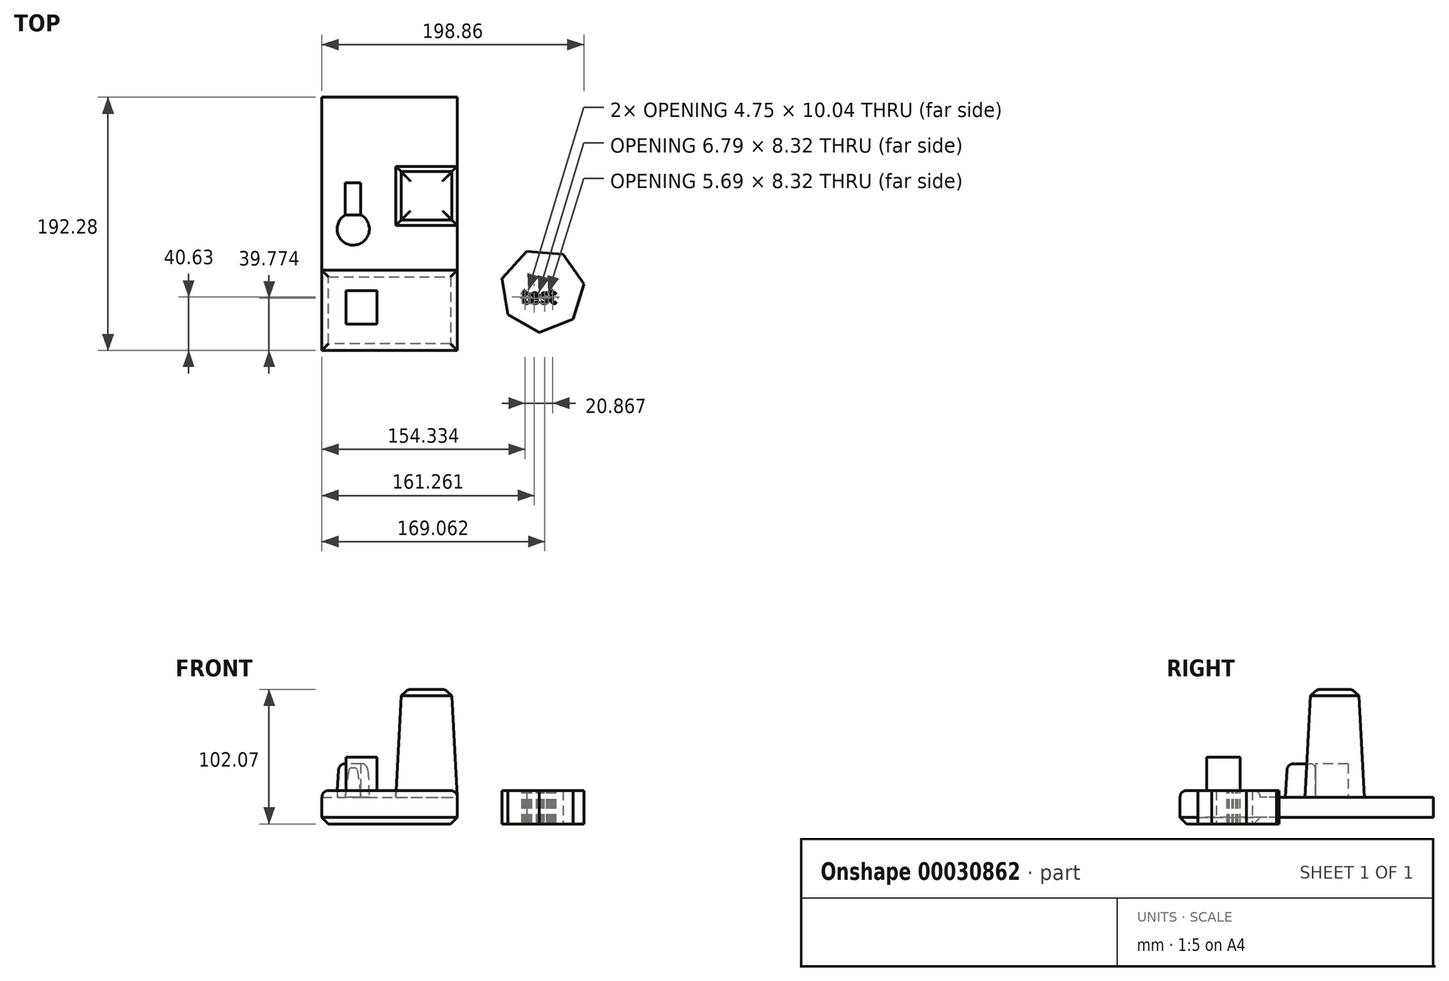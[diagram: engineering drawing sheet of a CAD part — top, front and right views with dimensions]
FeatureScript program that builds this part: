
annotation { "Feature Type Name" : "Feature", "Feature Type Description" : "" }
export const myFeature = defineFeature(function(context is Context, id is Id, definition is map)
    precondition{}
    {
        {
            var Q0;
            Q0=qCreatedBy(makeId("Top.planeOp"),FACE);
            var sketch = newSketch(context, id + "F0", { "sketchPlane" : qUnion([Q0])});
            skLineSegment(sketch, "E0.bottom", {"start": v(-102.72, 60.89) * mm, "end": v(0, 60.89) * mm});
            skLineSegment(sketch, "E0.top", {"start": v(-102.72, 0) * mm, "end": v(0, 0) * mm});
            skLineSegment(sketch, "E0.left", {"start": v(-102.72, 60.89) * mm, "end": v(-102.72, 0) * mm});
            skLineSegment(sketch, "E0.right", {"start": v(0, 60.89) * mm, "end": v(0, 0) * mm});
            skSolve(sketch);
        }
        {
            var Q0;
            Q0 = qSketchRegion(id + "F0", true);
            extrude(context, id + "F1", {"entities" : qUnion([Q0]), "depth" : 25.4 * mm});
        }
        {
            var Q0;
            Q0=makeQuery(id+"F1.opExtrude","CAP_EDGE",EDGE,{"disambiguationData":[OSD([sQuery(id+"F0.wireOp",EDGE,"E0.top")])],"isStart":false});
            var Q1;
            Q1=makeQuery(id+"F1.opExtrude","CAP_EDGE",EDGE,{"disambiguationData":[OSD([sQuery(id+"F0.wireOp",EDGE,"E0.left")])],"isStart":false});
            var Q2;
            Q2=makeQuery(id+"F1.opExtrude","CAP_EDGE",EDGE,{"disambiguationData":[OSD([sQuery(id+"F0.wireOp",EDGE,"E0.bottom")])],"isStart":false});
            var Q3;
            Q3=makeQuery(id+"F1.opExtrude","CAP_EDGE",EDGE,{"disambiguationData":[OSD([sQuery(id+"F0.wireOp",EDGE,"E0.right")])],"isStart":false});
            fillet(context, id + "F2", {"entities" : qUnion([Q0, Q1, Q2, Q3]), "radius" : 5.08 * mm, "tangentPropagation" : true, "allowEdgeOverflow" : false});
        }
        {
            var Q0;
            Q0=makeQuery(id+"F1.opExtrude","CAP_EDGE",EDGE,{"disambiguationData":[OSD([sQuery(id+"F0.wireOp",EDGE,"E0.top")])],"isStart":true});
            var Q1;
            Q1=makeQuery(id+"F1.opExtrude","CAP_FACE",FACE,{"disambiguationData":[OSD([sQuery(id+"F0.wireOp",EDGE,"E0.bottom"),sQuery(id+"F0.wireOp",EDGE,"E0.top"),sQuery(id+"F0.wireOp",EDGE,"E0.left"),sQuery(id+"F0.wireOp",EDGE,"E0.right")])],"isStart":true});
            chamfer(context, id + "F3", {"entities" : qUnion([Q0, Q1]), "width" : 5.08 * mm, "tangentPropagation" : true});
        }
        {
            var Q0;
            Q0=makeQuery(id+"F1.opExtrude","SWEPT_FACE",FACE,{"disambiguationData":[OSD([sQuery(id+"F0.wireOp",EDGE,"E0.bottom")])]});
            extrude(context, id + "F4", {"entities" : qUnion([Q0]), "operationType" : NewBodyOperationType.ADD, "depth" : 131.4 * mm});
        }
        {
            var Q0;
            {var subQ0=sQuery(id+"F0.wireOp",EDGE,"E0.bottom");Q0=makeQuery(id+"F4.opExtrude","SWEPT_FACE",FACE,{"disambiguationData":[OSD([subQ0]),TDD([makeQuery(id+"F2.opFillet","BLEND_EDGE",EDGE,{"blendedFrom":[makeQuery(id+"F1.opExtrude","CAP_EDGE",EDGE,{"disambiguationData":[OSD([subQ0])],"isStart":false}),makeQuery(id+"F1.opExtrude","SWEPT_FACE",FACE,{"disambiguationData":[OSD([subQ0])]})],"blendedInto":[makeQuery(id+"F1.opExtrude","SWEPT_FACE",FACE,{"disambiguationData":[OSD([subQ0])]})]})])]});}
            var sketch = newSketch(context, id + "F5", { "sketchPlane" : qUnion([Q0])});
            skLineSegment(sketch, "E1.bottom", {"start": v(-46.64, 139.86) * mm, "end": v(0, 139.86) * mm});
            skLineSegment(sketch, "E1.top", {"start": v(-46.64, 94.95) * mm, "end": v(0, 94.95) * mm});
            skLineSegment(sketch, "E1.left", {"start": v(0, 139.86) * mm, "end": v(0, 94.95) * mm});
            skLineSegment(sketch, "E1.right", {"start": v(-46.64, 139.86) * mm, "end": v(-46.64, 94.95) * mm});
            skSolve(sketch);
        }
        {
            var Q0;
            Q0 = qSketchRegion(id + "F5", true);
            extrude(context, id + "F6", {"entities" : qUnion([Q0]), "operationType" : NewBodyOperationType.ADD, "depth" : 81.75 * mm, "hasDraft" : true, "draftAngle" : 3 * degree, "draftPullDirection" : true});
        }
        {
            var Q0;
            Q0=makeQuery(id+"F6.opExtrude","CAP_EDGE",EDGE,{"disambiguationData":[OSD([sQuery(id+"F5.wireOp",EDGE,"E1.left")])],"isStart":false});
            var Q1;
            Q1=makeQuery(id+"F6.opExtrude","CAP_EDGE",EDGE,{"disambiguationData":[OSD([sQuery(id+"F5.wireOp",EDGE,"E1.top")])],"isStart":false});
            var Q2;
            Q2=makeQuery(id+"F6.opExtrude","CAP_EDGE",EDGE,{"disambiguationData":[OSD([sQuery(id+"F5.wireOp",EDGE,"E1.right")])],"isStart":false});
            var Q3;
            Q3=makeQuery(id+"F6.opExtrude","CAP_EDGE",EDGE,{"disambiguationData":[OSD([sQuery(id+"F5.wireOp",EDGE,"E1.bottom")])],"isStart":false});
            chamfer(context, id + "F7", {"entities" : qUnion([Q0, Q1, Q2, Q3]), "width" : 5.08 * mm, "tangentPropagation" : true});
        }
        {
            var Q0;
            {var subQ0=sQuery(id+"F5.wireOp",EDGE,"E1.top");Q0=makeQuery(id+"F7.opChamfer","BLEND_EDGE",EDGE,{"blendedFrom":[makeQuery(id+"F6.opExtrude","CAP_EDGE",EDGE,{"disambiguationData":[OSD([subQ0])],"isStart":false}),makeQuery(id+"F6.opExtrude","CAP_FACE",FACE,{"disambiguationData":[OSD([sQuery(id+"F5.wireOp",EDGE,"E1.bottom"),subQ0,sQuery(id+"F5.wireOp",EDGE,"E1.left"),sQuery(id+"F5.wireOp",EDGE,"E1.right")])],"isStart":false})],"blendedInto":[makeQuery(id+"F6.opExtrude","CAP_FACE",FACE,{"disambiguationData":[OSD([sQuery(id+"F5.wireOp",EDGE,"E1.bottom"),subQ0,sQuery(id+"F5.wireOp",EDGE,"E1.left"),sQuery(id+"F5.wireOp",EDGE,"E1.right")])],"isStart":false})]});}
            var Q1;
            {var subQ0=sQuery(id+"F5.wireOp",EDGE,"E1.left");Q1=makeQuery(id+"F7.opChamfer","BLEND_EDGE",EDGE,{"blendedFrom":[makeQuery(id+"F6.opExtrude","CAP_EDGE",EDGE,{"disambiguationData":[OSD([subQ0])],"isStart":false}),makeQuery(id+"F6.opExtrude","CAP_FACE",FACE,{"disambiguationData":[OSD([sQuery(id+"F5.wireOp",EDGE,"E1.bottom"),sQuery(id+"F5.wireOp",EDGE,"E1.top"),subQ0,sQuery(id+"F5.wireOp",EDGE,"E1.right")])],"isStart":false})],"blendedInto":[makeQuery(id+"F6.opExtrude","CAP_FACE",FACE,{"disambiguationData":[OSD([sQuery(id+"F5.wireOp",EDGE,"E1.bottom"),sQuery(id+"F5.wireOp",EDGE,"E1.top"),subQ0,sQuery(id+"F5.wireOp",EDGE,"E1.right")])],"isStart":false})]});}
            var Q2;
            {var subQ0=sQuery(id+"F5.wireOp",EDGE,"E1.bottom");Q2=makeQuery(id+"F7.opChamfer","BLEND_EDGE",EDGE,{"blendedFrom":[makeQuery(id+"F6.opExtrude","CAP_EDGE",EDGE,{"disambiguationData":[OSD([subQ0])],"isStart":false}),makeQuery(id+"F6.opExtrude","CAP_FACE",FACE,{"disambiguationData":[OSD([subQ0,sQuery(id+"F5.wireOp",EDGE,"E1.top"),sQuery(id+"F5.wireOp",EDGE,"E1.left"),sQuery(id+"F5.wireOp",EDGE,"E1.right")])],"isStart":false})],"blendedInto":[makeQuery(id+"F6.opExtrude","CAP_FACE",FACE,{"disambiguationData":[OSD([subQ0,sQuery(id+"F5.wireOp",EDGE,"E1.top"),sQuery(id+"F5.wireOp",EDGE,"E1.left"),sQuery(id+"F5.wireOp",EDGE,"E1.right")])],"isStart":false})]});}
            var Q3;
            {var subQ0=sQuery(id+"F5.wireOp",EDGE,"E1.right");Q3=makeQuery(id+"F7.opChamfer","BLEND_EDGE",EDGE,{"blendedFrom":[makeQuery(id+"F6.opExtrude","CAP_EDGE",EDGE,{"disambiguationData":[OSD([subQ0])],"isStart":false}),makeQuery(id+"F6.opExtrude","CAP_FACE",FACE,{"disambiguationData":[OSD([sQuery(id+"F5.wireOp",EDGE,"E1.bottom"),sQuery(id+"F5.wireOp",EDGE,"E1.top"),sQuery(id+"F5.wireOp",EDGE,"E1.left"),subQ0])],"isStart":false})],"blendedInto":[makeQuery(id+"F6.opExtrude","CAP_FACE",FACE,{"disambiguationData":[OSD([sQuery(id+"F5.wireOp",EDGE,"E1.bottom"),sQuery(id+"F5.wireOp",EDGE,"E1.top"),sQuery(id+"F5.wireOp",EDGE,"E1.left"),subQ0])],"isStart":false})]});}
            fillet(context, id + "F8", {"entities" : qUnion([Q0, Q1, Q2, Q3]), "radius" : 5.08 * mm, "tangentPropagation" : true, "allowEdgeOverflow" : false});
        }
        {
            var Q0;
            {var subQ0=sQuery(id+"F0.wireOp",EDGE,"E0.bottom");Q0=makeQuery(id+"F4.opExtrude","SWEPT_FACE",FACE,{"disambiguationData":[OSD([subQ0]),TDD([makeQuery(id+"F2.opFillet","BLEND_EDGE",EDGE,{"blendedFrom":[makeQuery(id+"F1.opExtrude","CAP_EDGE",EDGE,{"disambiguationData":[OSD([subQ0])],"isStart":false}),makeQuery(id+"F1.opExtrude","SWEPT_FACE",FACE,{"disambiguationData":[OSD([subQ0])]})],"blendedInto":[makeQuery(id+"F1.opExtrude","SWEPT_FACE",FACE,{"disambiguationData":[OSD([subQ0])]})]})])]});}
            var sketch = newSketch(context, id + "F9", { "sketchPlane" : qUnion([Q0])});
            skCircle(sketch, "E2", {"center": v(-79, 92.24) * mm, "radius": 12.24 * mm});
            skSolve(sketch);
        }
        {
            var Q0;
            Q0 = qSketchRegion(id + "F9", true);
            extrude(context, id + "F10", {"entities" : qUnion([Q0]), "operationType" : NewBodyOperationType.ADD, "depth" : 25.4 * mm, "hasDraft" : true, "draftAngle" : 3 * degree, "draftPullDirection" : true});
        }
        {
            var Q0;
            Q0=makeQuery(id+"F10.opExtrude","CAP_EDGE",EDGE,{"disambiguationData":[OSD([sQuery(id+"F9.wireOp",EDGE,"E2")])],"isStart":false});
            fillet(context, id + "F11", {"entities" : qUnion([Q0]), "radius" : 5.08 * mm, "tangentPropagation" : true, "allowEdgeOverflow" : false});
        }
        {
            var Q0;
            Q0=makeQuery(id+"F1.opExtrude","CAP_FACE",FACE,{"disambiguationData":[OSD([sQuery(id+"F0.wireOp",EDGE,"E0.bottom"),sQuery(id+"F0.wireOp",EDGE,"E0.top"),sQuery(id+"F0.wireOp",EDGE,"E0.left"),sQuery(id+"F0.wireOp",EDGE,"E0.right")])],"isStart":false});
            var sketch = newSketch(context, id + "F12", { "sketchPlane" : qUnion([Q0])});
            skLineSegment(sketch, "E3.bottom", {"start": v(-84.42, 20.12) * mm, "end": v(-60.82, 20.12) * mm});
            skLineSegment(sketch, "E3.top", {"start": v(-84.42, 45.44) * mm, "end": v(-60.82, 45.44) * mm});
            skLineSegment(sketch, "E3.left", {"start": v(-84.42, 20.12) * mm, "end": v(-84.42, 45.44) * mm});
            skLineSegment(sketch, "E3.right", {"start": v(-60.82, 20.12) * mm, "end": v(-60.82, 45.44) * mm});
            skSolve(sketch);
        }
        {
            var Q0;
            Q0 = qSketchRegion(id + "F12", true);
            extrude(context, id + "F13", {"entities" : qUnion([Q0]), "depth" : 25.4 * mm});
        }
        {
            var Q0;
            Q0=qCreatedBy(makeId("Top.planeOp"),FACE);
            var sketch = newSketch(context, id + "F14", { "sketchPlane" : qUnion([Q0])});
            skCircle(sketch, "E4.cCircle", {"center": v(64.61, 45.48) * mm, "radius": 28.75 * mm, "construction": true});
            skLineSegment(sketch, "E4.0", {"start": v(96.14, 50.4) * mm, "end": v(88.12, 23.9) * mm});
            skLineSegment(sketch, "E4.1", {"start": v(88.12, 23.9) * mm, "end": v(62.4, 13.65) * mm});
            skLineSegment(sketch, "E4.2", {"start": v(62.4, 13.65) * mm, "end": v(38.34, 27.37) * mm});
            skLineSegment(sketch, "E4.3", {"start": v(38.34, 27.37) * mm, "end": v(34.07, 54.73) * mm});
            skLineSegment(sketch, "E4.4", {"start": v(34.07, 54.73) * mm, "end": v(52.8, 75.13) * mm});
            skLineSegment(sketch, "E4.5", {"start": v(52.8, 75.13) * mm, "end": v(80.42, 73.2) * mm});
            skLineSegment(sketch, "E4.6", {"start": v(80.42, 73.2) * mm, "end": v(96.14, 50.4) * mm});
            skPoint(sketch, "E4.0.midPoint", {"position": v(92.13, 37.15) * mm});
            skSolve(sketch);
        }
        {
            var Q0;
            Q0 = qSketchRegion(id + "F14", true);
            extrude(context, id + "F15", {"entities" : qUnion([Q0]), "depth" : 25.4 * mm});
        }
        {
            var Q0;
            Q0=makeQuery(id+"F15.opExtrude","CAP_FACE",FACE,{"disambiguationData":[OSD([sQuery(id+"F14.wireOp",EDGE,"E4.0"),sQuery(id+"F14.wireOp",EDGE,"E4.1"),sQuery(id+"F14.wireOp",EDGE,"E4.2"),sQuery(id+"F14.wireOp",EDGE,"E4.3"),sQuery(id+"F14.wireOp",EDGE,"E4.4"),sQuery(id+"F14.wireOp",EDGE,"E4.5"),sQuery(id+"F14.wireOp",EDGE,"E4.6")])],"isStart":false});
            var sketch = newSketch(context, id + "F16", { "sketchPlane" : qUnion([Q0])});
            skText(sketch, "E5", { "text": "test\n", "fontName": "OpenSans-Regular.ttf"});
            const initialGuessF16  = {"E5": [0.04901, 0.03576, 1, 0, 0.0108]};
            skSetInitialGuess(sketch, initialGuessF16);
            skSolve(sketch);
        }
        {
            var Q0;
            Q0 = qSketchRegion(id + "F16", true);
            extrude(context, id + "F17", {"entities" : qUnion([Q0]), "operationType" : NewBodyOperationType.REMOVE, "endBound" : BoundingType.THROUGH_ALL, "oppositeDirection" : true, "depth" : 25.4 * mm});
        }
        {
            var Q0;
            {var subQ0=sQuery(id+"F0.wireOp",EDGE,"E0.bottom");Q0=makeQuery(id+"F4.opExtrude","SWEPT_FACE",FACE,{"disambiguationData":[OSD([subQ0]),TDD([makeQuery(id+"F2.opFillet","BLEND_EDGE",EDGE,{"blendedFrom":[makeQuery(id+"F1.opExtrude","CAP_EDGE",EDGE,{"disambiguationData":[OSD([subQ0])],"isStart":false}),makeQuery(id+"F1.opExtrude","SWEPT_FACE",FACE,{"disambiguationData":[OSD([subQ0])]})],"blendedInto":[makeQuery(id+"F1.opExtrude","SWEPT_FACE",FACE,{"disambiguationData":[OSD([subQ0])]})]})])]});}
            var sketch = newSketch(context, id + "F18", { "sketchPlane" : qUnion([Q0])});
            skLineSegment(sketch, "E6.bottom", {"start": v(-73.2, 127.49) * mm, "end": v(-85.02, 127.49) * mm});
            skLineSegment(sketch, "E6.top", {"start": v(-73.2, 102.9) * mm, "end": v(-85.02, 102.9) * mm});
            skLineSegment(sketch, "E6.left", {"start": v(-73.2, 127.49) * mm, "end": v(-73.2, 102.9) * mm});
            skLineSegment(sketch, "E6.right", {"start": v(-85.02, 127.49) * mm, "end": v(-85.02, 102.9) * mm});
            skSolve(sketch);
        }
        {
            var Q0;
            Q0 = qSketchRegion(id + "F18", true);
            extrude(context, id + "F19", {"entities" : qUnion([Q0]), "operationType" : NewBodyOperationType.ADD, "depth" : 25.4 * mm});
        }
    });
